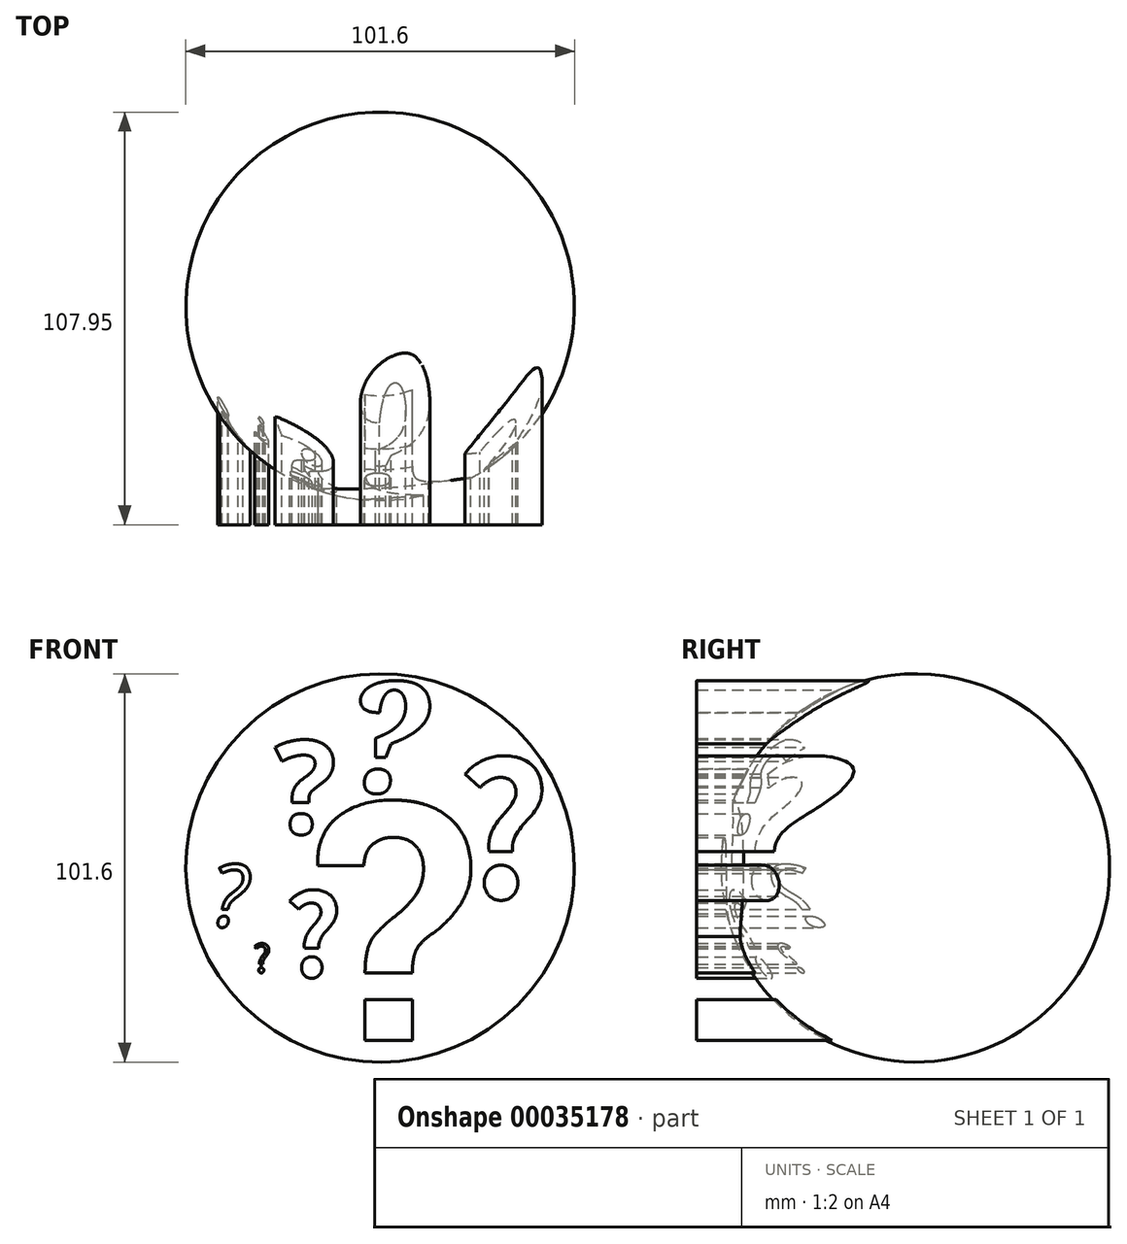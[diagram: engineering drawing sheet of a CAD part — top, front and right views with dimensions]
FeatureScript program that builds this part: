
annotation { "Feature Type Name" : "Feature", "Feature Type Description" : "" }
export const myFeature = defineFeature(function(context is Context, id is Id, definition is map)
    precondition{}
    {
        {
            var Q0;
            Q0=qCreatedBy(makeId("Front.planeOp"),FACE);
            var sketch = newSketch(context, id + "F0", { "sketchPlane" : qUnion([Q0])});
            skArc(sketch, "E0", {"start": v(-87.47, -0.32) * mm, "mid": v(-15.63, 0.14) * mm, "end": v(-16.09, 71.98) * mm});
            skLineSegment(sketch, "E1", {"start": v(-87.47, -0.32) * mm, "end": v(-16.09, 71.98) * mm});
            skSolve(sketch);
        }
        {
            var Q0;
            Q0=makeQuery(id+"F0.imprint","IMPRINT",FACE,{"disambiguationData":[TD([[makeQuery(id+"F0.imprint","IMPRINT",EDGE,{"derivedFrom":sQuery(id+"F0.wireOp",EDGE,"E0")}),1.0]])]});
            var Q1;
            Q1=sQuery(id+"F0.wireOp",EDGE,"E1");
            revolve(context, id + "F1", {"entities" : qUnion([Q0]), "axis" : qUnion([Q1]), "revolveType" : RevolveType.FULL});
        }
        {
            var Q0;
            Q0=qCreatedBy(makeId("Front.planeOp"),FACE);
            var sketch = newSketch(context, id + "F2", { "sketchPlane" : qUnion([Q0])});
            skText(sketch, "E2", { "text": "?", "fontName": "OpenSans-Bold.ttf"});
            skText(sketch, "E3", { "text": "?", "fontName": "RobotoSlab-Bold.ttf"});
            skText(sketch, "E4", { "text": "?", "fontName": "NotoSansCJKsc-Bold.otf"});
            skText(sketch, "E5", { "text": "?", "fontName": "OpenSans-Italic.ttf"});
            skText(sketch, "E6", { "text": "?", "fontName": "NotoSerif-BoldItalic.ttf"});
            skText(sketch, "E7", { "text": "?", "fontName": "NotoSansCJKjp-Regular.otf"});
            skText(sketch, "E8", { "text": "?", "fontName": "NotoSansCJKsc-Bold.otf"});
            const initialGuessF2  = {"E2": [-0.07937, 0.04486, 1, 0, 0.02442], "E3": [-0.0696, -0.00925, 1, 0, 0.06272], "E4": [-0.0318, 0.02798, 1, 0, 0.03465], "E5": [-0.09596, 0.02053, 1, 0, 0.01632], "E6": [-0.06102, 0.05547, 1, 0, 0.02921], "E7": [-0.08507, 0.0085, 1, 0, 0.00716], "E8": [-0.07677, 0.00736, 1, 0, 0.0212]};
            skSetInitialGuess(sketch, initialGuessF2);
            skSolve(sketch);
        }
        {
            var Q0;
            Q0 = qSketchRegion(id + "F2", true);
            extrude(context, id + "F3", {"entities" : qUnion([Q0]), "operationType" : NewBodyOperationType.ADD, "depth" : 57.15 * mm});
        }
    });
